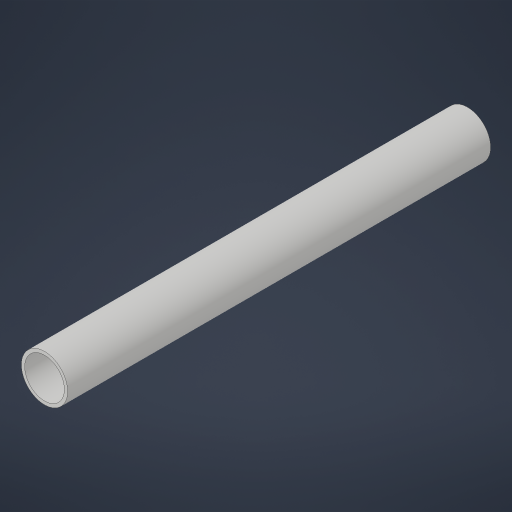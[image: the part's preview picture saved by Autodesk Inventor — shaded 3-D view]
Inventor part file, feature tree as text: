
AUTODESK INVENTOR PART (.ipt)
format: ipt  version: 2023.4 (Build 274418000, 418)  size: 168,448 bytes
history: native  units: in
note: dims shown in document units (in); Inventor stores cm internally (conversion verified against a paired STEP export)
features: extrude x1, sketch x1
ambient origin geometry x8: Origin, YZ Plane, XZ Plane, XY Plane, X Axis, Y Axis, Z Axis, Center Point
bodies: Solid1 (feature_tree)
feature tree (2):
  extrude  "Extrusion1"  Depth=8.0in TaperAngle=0.0deg
  sketch  "Sketch1"  dims[d0=0.875in d1=8.0in d2=0.0in d3=0.0625in]
